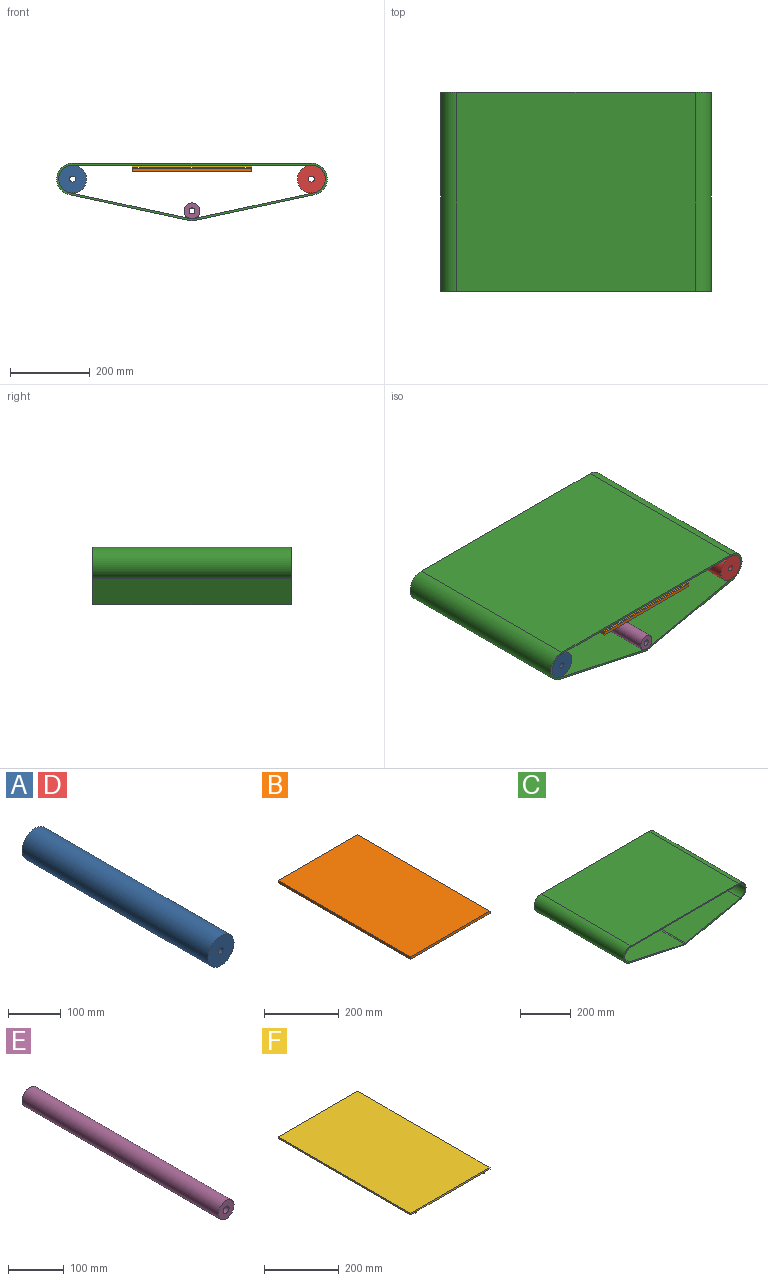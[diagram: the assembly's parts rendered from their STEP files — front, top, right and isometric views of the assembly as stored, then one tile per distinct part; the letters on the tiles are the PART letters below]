
ASSEMBLY  parts=6 mates=11
PART A: 4 faces, bbox 70x500x70 mm
  f0: cylinder r=35mm len=500mm, axis (0,-1,0), area 109955.7mm2, adj f1,f2
  f1: plane 70x70mm, normal (0,1,0), area 3671.7mm2, adj f0,f3
  f2: plane 70x70mm, normal (0,-1,0), area 3671.7mm2, adj f0,f3
  f3: cylinder r=7.5mm len=500mm, axis (0,-1,0), area 23561.9mm2, adj f1,f2
PART B: 6 faces, bbox 300x500x8 mm
  f0: plane 500x300mm, normal (0,0,-1), area 150000mm2, adj f1,f3,f4,f5
  f1: plane 500x8mm, normal (1,0,0), area 4000mm2, adj f0,f2,f4,f5
  f2: plane 500x300mm, normal (0,0,1), area 150000mm2, adj f1,f3,f4,f5
  f3: plane 500x8mm, normal (-1,0,0), area 4000mm2, adj f0,f2,f4,f5
  f4: plane 300x8mm, normal (0,1,0), area 2400mm2, adj f0,f1,f2,f3
  f5: plane 300x8mm, normal (0,-1,0), area 2400mm2, adj f0,f1,f2,f3
PART C: 14 faces, bbox 680x500x145 mm
  f0: plane 600x500mm, normal (0,0,1), area 300000mm2, adj f1,f11,f12,f13
  f1: cylinder r=40mm len=500mm, axis (0,-1,0), area 58586.4mm2, adj f0,f2,f12,f13
  f2: plane 500x303.16mm, normal (-0.21,0,-0.98), area 155060.5mm2, adj f1,f3,f12,f13
  f3: cylinder r=25mm len=500mm, axis (0,-1,0), area 5306.8mm2, adj f2,f4,f12,f13
  f4: plane 500x303.16mm, normal (0.21,0,-0.98), area 155060.5mm2, adj f3,f11,f12,f13
  f5: cylinder r=35mm len=500mm, axis (0,-1,0), area 51263.1mm2, adj f6,f10,f12,f13
  f6: plane 500x303.16mm, normal (-0.21,0,0.98), area 155060.5mm2, adj f5,f7,f12,f13
  f7: cylinder r=20mm len=500mm, axis (0,-1,0), area 4245.4mm2, adj f6,f8,f12,f13
  f8: plane 500x303.16mm, normal (0.21,0,0.98), area 155060.5mm2, adj f7,f9,f12,f13
  f9: cylinder r=35mm len=500mm, axis (0,-1,0), area 51263.1mm2, adj f8,f10,f12,f13
  f10: plane 600x500mm, normal (0,0,-1), area 300000mm2, adj f5,f9,f12,f13
  f11: cylinder r=40mm len=500mm, axis (0,-1,0), area 58586.4mm2, adj f0,f4,f12,f13
  f12: plane 680x145mm, normal (0,1,0), area 7247.5mm2, adj f0,f1,f2,f3,f4,f5,f6,f7
  f13: plane 680x145mm, normal (0,-1,0), area 7247.5mm2, adj f0,f1,f2,f3,f4,f5,f6,f7
PART D: same geometry as A
PART E: 4 faces, bbox 40x500x40 mm
  f0: cylinder r=20mm len=500mm, axis (0,-1,0), area 62831.9mm2, adj f1,f2
  f1: plane 40x40mm, normal (0,1,0), area 1079.9mm2, adj f0,f3
  f2: plane 40x40mm, normal (0,-1,0), area 1079.9mm2, adj f0,f3
  f3: cylinder r=7.5mm len=500mm, axis (0,-1,0), area 23561.9mm2, adj f1,f2
PART F: 14 faces, bbox 300x500x9 mm
  f0: plane 500x20mm, normal (0,0,-1), area 10000mm2, adj f4,f6,f7,f11
  f1: plane 500x252mm, normal (0,0,-1), area 126000mm2, adj f6,f7,f10,f12
  f2: plane 500x5mm, normal (-1,0,0), area 2500mm2, adj f3,f5,f6,f7
  f3: plane 500x20mm, normal (0,0,-1), area 10000mm2, adj f2,f6,f7,f8
  f4: plane 500x5mm, normal (1,0,0), area 2500mm2, adj f0,f5,f6,f7
  f5: plane 500x300mm, normal (0,0,1), area 150000mm2, adj f2,f4,f6,f7
  f6: plane 300x9mm, normal (0,1,0), area 1532mm2, adj f0,f1,f2,f3,f4,f5,f8,f9
  f7: plane 300x9mm, normal (0,-1,0), area 1532mm2, adj f0,f1,f2,f3,f4,f5,f8,f9
  f8: plane 500x4mm, normal (-1,0,0), area 2000mm2, adj f3,f6,f7,f9
  f9: plane 500x4mm, normal (0,0,-1), area 2000mm2, adj f6,f7,f8,f10
  f10: plane 500x4mm, normal (1,0,0), area 2000mm2, adj f1,f6,f7,f9
  f11: plane 500x4mm, normal (1,0,0), area 2000mm2, adj f0,f6,f7,f13
  f12: plane 500x4mm, normal (-1,0,0), area 2000mm2, adj f1,f6,f7,f13
  f13: plane 500x4mm, normal (0,0,-1), area 2000mm2, adj f6,f7,f11,f12
PLACE A t=(-612.22,-618.08,244.8)mm
PLACE B t=(-312.22,-618.08,262.8)mm
PLACE C t=(-312.22,-618.08,244.8)mm
PLACE D t=(-12.22,-618.08,244.8)mm
PLACE E t=(-312.22,-618.08,164.8)mm
PLACE F t=(-312.22,-618.08,274.8)mm
MATE planar B.f2 <-> F.f13  axis (0,0,1) through (-312.22,-368.08,270.8)mm
MATE planar F.f5 <-> C.f10  axis (0,0,1) through (-312.22,-368.08,279.8)mm
MATE planar B.f5 <-> C.f13  axis (0,-1,0) through (-312.22,-618.08,266.8)mm
MATE planar C.f13 <-> A.f0  axis (0,-1,0) through (-312.22,-618.08,230.39)mm
MATE cylindrical D.f0 <-> C.f5  axis (0,-1,0) through (-12.22,-368.08,244.8)mm
MATE planar B.f5 <-> F.f7  axis (0,-1,0) through (-312.22,-618.08,266.8)mm
MATE planar A.f0 <-> D.f0  axis (0,-1,0) through (-612.22,-618.08,244.8)mm
MATE cylindrical E.f0 <-> C.f7  axis (0,-1,0) through (-312.22,-368.08,164.8)mm
MATE cylindrical A.f0 <-> C.f9  axis (0,-1,0) through (-612.22,-368.08,244.8)mm
MATE planar B.f1 <-> F.f4  axis (1,0,0) through (-162.22,-368.08,266.8)mm
MATE planar D.f0 <-> E.f0  axis (0,-1,0) through (-12.22,-618.08,244.8)mm
